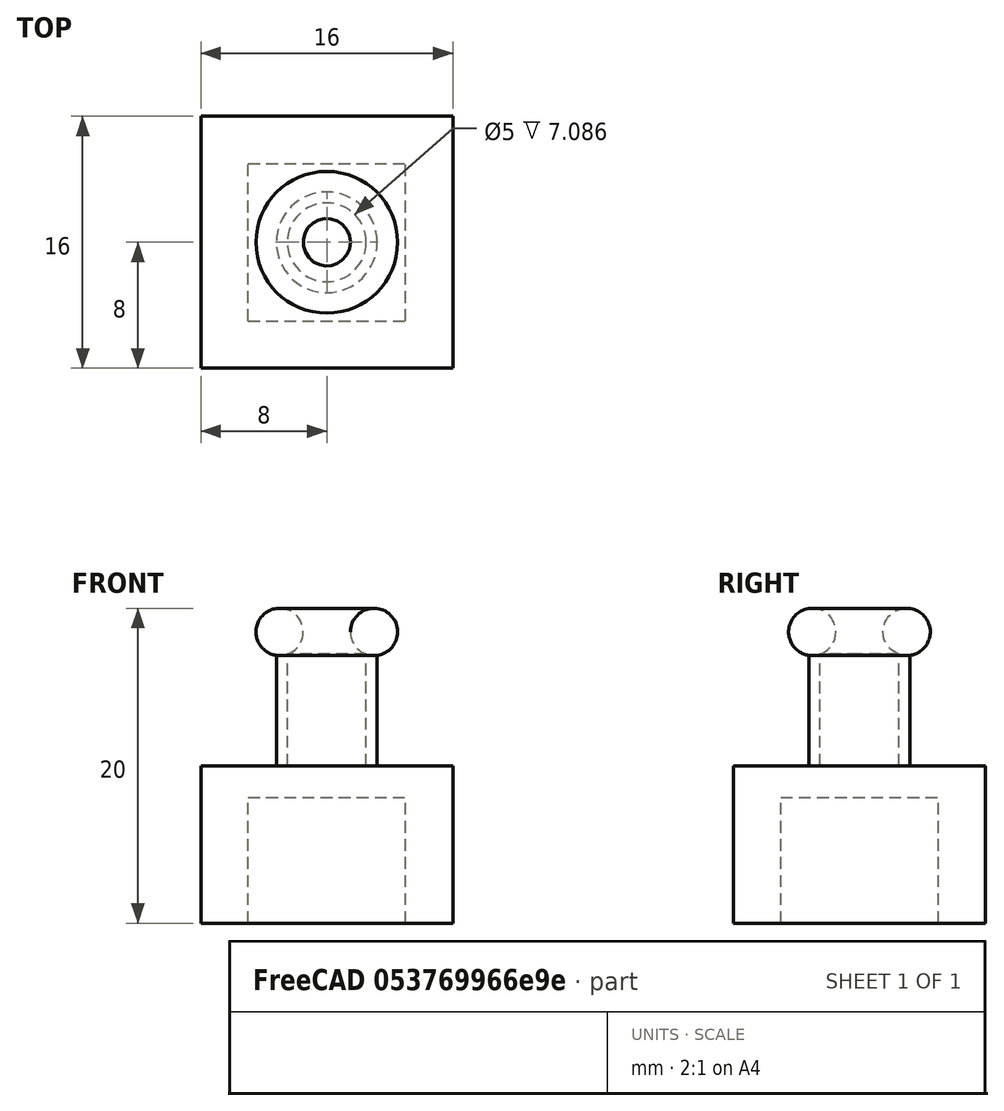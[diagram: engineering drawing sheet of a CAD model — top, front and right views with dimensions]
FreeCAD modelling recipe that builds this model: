
FCSTD DOCUMENT  (FreeCAD 0.18.3R)
Label: torus
License: All rights reserved
LicenseURL: http://en.wikipedia.org/wiki/All_rights_reserved
objects: Part::Box×2, Part::Cylinder×2, Part::Cut×2, Part::Torus×1, Part::MultiFuse×1
note: 8 computed .brp shape members not serialized (recipe doc carries the construction recipe); baked Part::Feature solids carry a one-line shape summary decoded from their .brp

FEATURE [Part::Box] Box  label="Cube"
  AttacherType = Attacher::AttachEngine3D
  Height = 10
  Length = 16
  Placement = pos=(-8,-8,0) rot=(0,0,1;0rad)
  Width = 16
FEATURE [Part::Cylinder] Cylinder
  Angle = 360
  AttacherType = Attacher::AttachEngine3D
  Height = 9
  Placement = pos=(0,0,10) rot=(0,0,1;0rad)
  Radius = 2.5
FEATURE [Part::Cylinder] Cylinder001
  Angle = 360
  AttacherType = Attacher::AttachEngine3D
  Height = 9
  Placement = pos=(0,0,10) rot=(0,0,1;0rad)
  Radius = 3.2
FEATURE [Part::Cut] Cut
  Base = -> Cylinder001
  Tool = -> Cylinder
FEATURE [Part::Torus] Torus
  Angle1 = -180
  Angle2 = 180
  Angle3 = 360
  AttacherType = Attacher::AttachEngine3D
  Placement = pos=(0,0,18.5) rot=(0,0,1;0rad)
  Radius1 = 3
  Radius2 = 1.5
FEATURE [Part::MultiFuse] Fusion
  Shapes = -> [Cut,Box,Torus]
FEATURE [Part::Box] Box001  label="Cube001"
  AttacherType = Attacher::AttachEngine3D
  Height = 8
  Length = 10
  Placement = pos=(-5,-5,0) rot=(0,0,1;0rad)
  Width = 10
FEATURE [Part::Cut] Cut001
  Base = -> Fusion
  Tool = -> Box001
